# Revit family: P350209-031-30
name_source: partatom
category: Lighting Fixtures
units: mm (PartAtom-declared; Revit-internal decimal feet)

## family parameters
Cut with Voids When Loaded = No
Host = Face
Light Source = No
OmniClass Number = 23.80.70.11.14.17
OmniClass Title = Direct/Indirect
Part Type = Normal
Room Calculation Point = No
Round Connector Dimension = Use Diameter
Shared = Yes

## types (1)
- P350209-031-30
    Apparent Load = 25 VA
    Assembly Code = D5020200
    Connector Description = Lighting Connector
    Default Elevation = 48 "
    Description = Quadrant LED Collection Four-Light Matte Black Modern Style Flush Mount Ceiling or Wall Light
    Features = Application: Define space with a minimalist approach with the Quadrant LED Collection 4-Light Matte Black Frosted Glass Modern Flush Mount Ceiling Light ideal for any hallway, stairwell, entryway, kitchen, or sitting room.
Styles: Perfect for modern and contemporary style settings.
Finish: Metal struts coated in a classic matte black finish are arranged in a modern geometric design giving the layered frame an impression of substance in space.
Materials: Constructed from steel to ensure a long product lifespan.
Glass/Shades: Integrated LED lights tip the end of the metal struts and glow from within the crisp frosted glass shades that create airy illumination.
Bulbs: For ideal illumination, 4 integrated LED modules are included (24w). 3000K. 90CRI. 1261 delivered lumens. Dimmable.
Dimensions: Measures 20-inch diameter by 4-inch height.
Certifications: cETLus damp location listed, meets California Title 24 JA8-2019.
Pairs With: Pairs with a variety of Progress Lighting fixtures.
Warranty: Our 5-year Limited Warranty guarantees your complete satisfaction with your purchase and includes professional after-sales customer service support.
    Fixture distribution = Direct
    Glass = Paint - Hubbell - White Texture
    Gold = Hubbell Metal Vintage Brass
    Housing Material = Paint - Hubbell - Textured Camera Black
    Lamp = LED/CFL/incandescent
    Load Classification = Lighting
    Manufacturer = Progress Lighting
    Model = P350209-031-30
    Power Factor = 1
    Product Documentation Link = https://hubbellcdn.com
    Product Link = https://www.hubbell.com
    URL = https://www.hubbell.com
    Voltage = 120 V
    Warranty = 5 years Warranty
    Wattage Comments = 25W
    Watts = 25 W
    Widh = 26 "
    Wood = Hubbell Gray

## geometry (parser evidence)
native form markers: Sweep x6
no freeform markers — native parametric forms only
